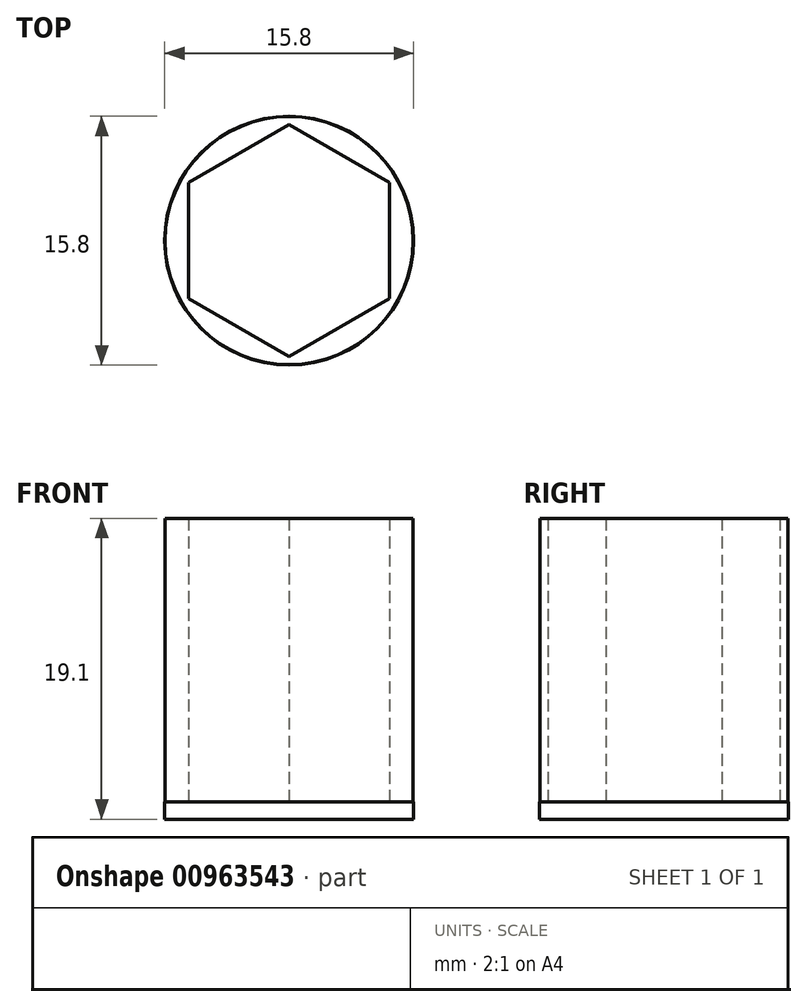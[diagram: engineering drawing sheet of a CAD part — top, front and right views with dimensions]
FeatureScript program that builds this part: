
annotation { "Feature Type Name" : "Feature", "Feature Type Description" : "" }
export const myFeature = defineFeature(function(context is Context, id is Id, definition is map)
    precondition{}
    {
        {
            var Q0;
            Q0=qCreatedBy(makeId("Top.planeOp"),FACE);
            var sketch = newSketch(context, id + "F0", { "sketchPlane" : qUnion([Q0])});
            skCircle(sketch, "E0.cCircle", {"center": v(0, 0) * mm, "radius": 6.38 * mm, "construction": true});
            skLineSegment(sketch, "E0.0", {"start": v(6.38, 3.68) * mm, "end": v(6.38, -3.68) * mm});
            skLineSegment(sketch, "E0.1", {"start": v(6.38, -3.68) * mm, "end": v(0, -7.37) * mm});
            skLineSegment(sketch, "E0.2", {"start": v(0, -7.37) * mm, "end": v(-6.38, -3.68) * mm});
            skLineSegment(sketch, "E0.3", {"start": v(-6.38, -3.68) * mm, "end": v(-6.38, 3.68) * mm});
            skLineSegment(sketch, "E0.4", {"start": v(-6.38, 3.68) * mm, "end": v(0, 7.37) * mm});
            skLineSegment(sketch, "E0.5", {"start": v(0, 7.37) * mm, "end": v(6.38, 3.68) * mm});
            skPoint(sketch, "E0.0.midPoint", {"position": v(6.38, 0) * mm});
            skCircle(sketch, "E1.0", {"center": v(0, 0) * mm, "radius": 7.88 * mm});
            skSolve(sketch);
        }
        {
            var Q0;
            Q0=makeQuery(id+"F0.imprint","IMPRINT",FACE,{"disambiguationData":[TD([[makeQuery(id+"F0.imprint","IMPRINT",EDGE,{"derivedFrom":sQuery(id+"F0.wireOp",EDGE,"E0.0")}),1.0]])]});
            extrude(context, id + "F1", {"entities" : qUnion([Q0]), "depth" : 18 * mm, "offsetDistance" : 25 * mm});
        }
        {
            var Q0;
            Q0=qCreatedBy(makeId("Top.planeOp"),FACE);
            var sketch = newSketch(context, id + "F2", { "sketchPlane" : qUnion([Q0])});
            skCircle(sketch, "E2", {"center": v(0, 0) * mm, "radius": 7.9 * mm});
            skSolve(sketch);
        }
        {
            var Q0;
            Q0 = qSketchRegion(id + "F2", true);
            extrude(context, id + "F3", {"entities" : qUnion([Q0]), "operationType" : NewBodyOperationType.ADD, "oppositeDirection" : true, "depth" : 1.1 * mm, "offsetDistance" : 25 * mm});
        }
    });
